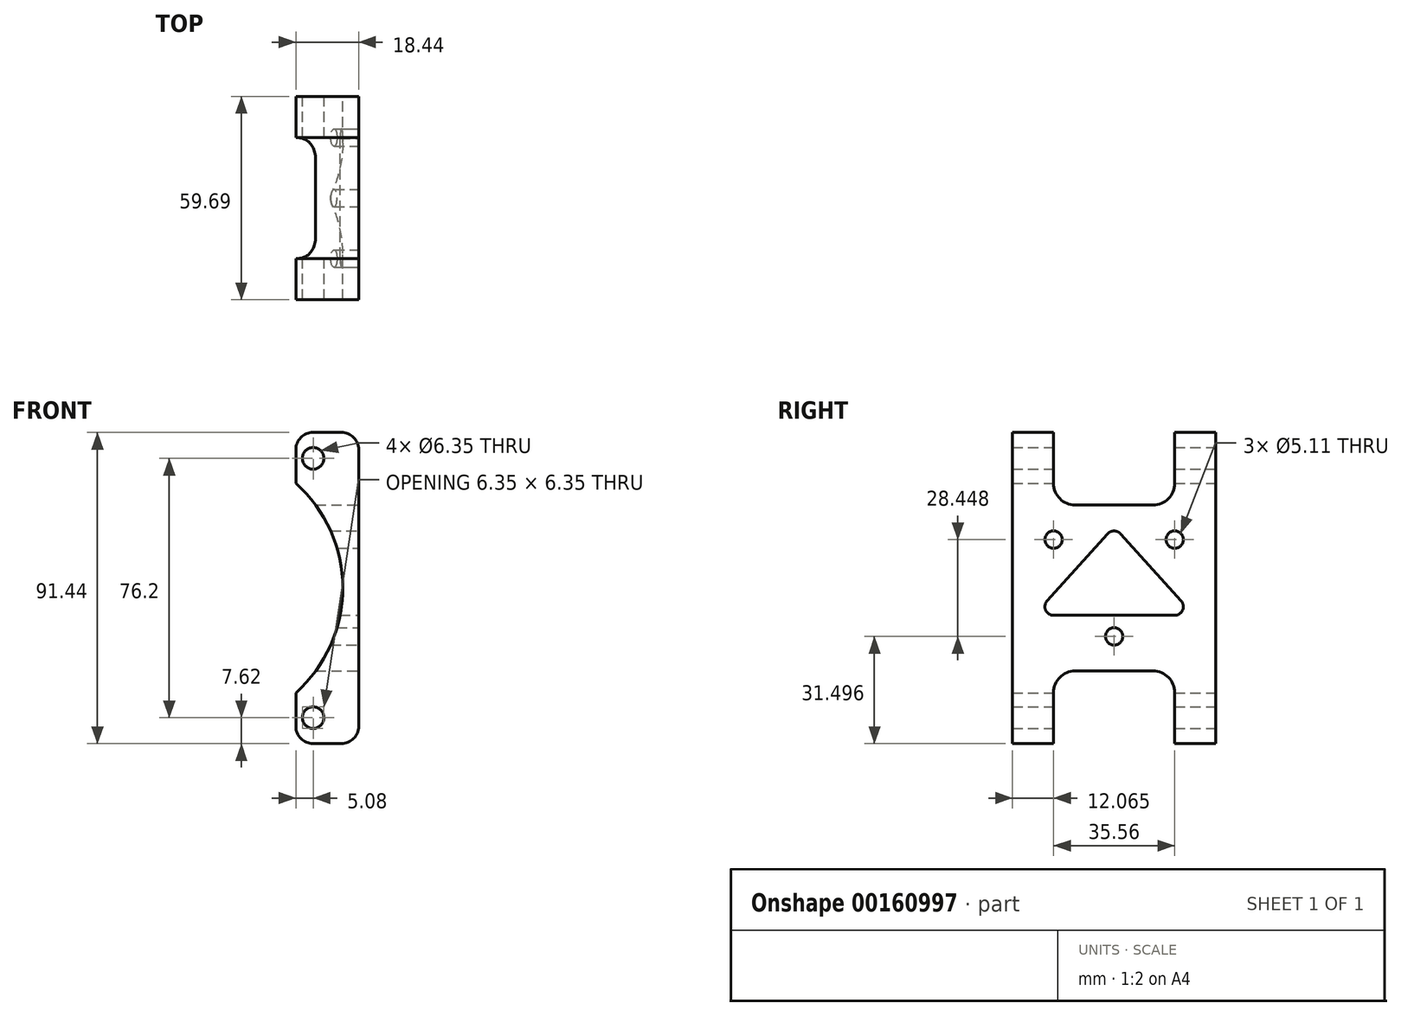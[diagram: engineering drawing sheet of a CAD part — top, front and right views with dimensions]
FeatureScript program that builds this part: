
annotation { "Feature Type Name" : "Feature", "Feature Type Description" : "" }
export const myFeature = defineFeature(function(context is Context, id is Id, definition is map)
    precondition{}
    {
        {
            var Q0;
            Q0=qCreatedBy(makeId("Front.planeOp"),FACE);
            var sketch = newSketch(context, id + "F0", { "sketchPlane" : qUnion([Q0])});
            skLineSegment(sketch, "E0.bottom", {"start": v(0, 0) * mm, "end": v(18.44, 0) * mm});
            skLineSegment(sketch, "E0.top", {"start": v(0, 91.44) * mm, "end": v(18.44, 91.44) * mm});
            skLineSegment(sketch, "E0.left", {"start": v(0, 0) * mm, "end": v(0, 19.33) * mm});
            skLineSegment(sketch, "E0.right", {"start": v(18.44, 0) * mm, "end": v(18.44, 91.44) * mm});
            skCircle(sketch, "E1", {"center": v(5.08, 83.82) * mm, "radius": 3.18 * mm});
            skCircle(sketch, "E2", {"center": v(5.08, 7.62) * mm, "radius": 3.18 * mm});
            skCircle(sketch, "E3", {"center": v(-27.48, 45.72) * mm, "radius": 38.1 * mm, "construction": true});
            skPoint(sketch, "E4.startSnap0", {"position": v(9.22, 91.44) * mm});
            skPoint(sketch, "E4.endSnap0", {"position": v(9.22, 0) * mm});
            skPoint(sketch, "E5", {"position": v(5.08, 45.72) * mm});
            skLineSegment(sketch, "E6", {"start": v(5.08, 83.82) * mm, "end": v(5.08, 7.62) * mm, "construction": true});
            skArc(sketch, "E7", {"start": v(0, 14.93) * mm, "mid": v(13.8, 45.72) * mm, "end": v(0, 76.51) * mm});
            skLineSegment(sketch, "E8.trimOffspring", {"start": v(0, 72.1) * mm, "end": v(0, 91.44) * mm});
            skSolve(sketch);
        }
        {
            var Q0;
            Q0 = qSketchRegion(id + "F0", true);
            extrude(context, id + "F1", {"entities" : qUnion([Q0]), "depth" : 59.69 * mm});
        }
        {
            var Q0;
            Q0=makeQuery(id+"F1.opExtrude","SWEPT_EDGE",EDGE,{"disambiguationData":[OSD([sQuery(id+"F0.wireOp",EDGE,"E0.top"),sQuery(id+"F0.wireOp",EDGE,"E8.trimOffspring")])]});
            var Q1;
            Q1=makeQuery(id+"F1.opExtrude","SWEPT_EDGE",EDGE,{"disambiguationData":[OSD([sQuery(id+"F0.wireOp",EDGE,"E0.bottom"),sQuery(id+"F0.wireOp",EDGE,"E0.left")])]});
            fillet(context, id + "F2", {"entities" : qUnion([Q0, Q1]), "radius" : 5.08 * mm, "tangentPropagation" : true, "allowEdgeOverflow" : false});
        }
        {
            var Q0;
            Q0=makeQuery(id+"F1.opExtrude","SWEPT_FACE",FACE,{"disambiguationData":[OSD([sQuery(id+"F0.wireOp",EDGE,"E0.right")])]});
            var sketch = newSketch(context, id + "F3", { "sketchPlane" : qUnion([Q0])});
            skLineSegment(sketch, "E9", {"start": v(-59.7, 45.72) * mm, "end": v(0, 45.72) * mm, "construction": true});
            skLineSegment(sketch, "E10", {"start": v(-29.85, 91.44) * mm, "end": v(-29.85, 0) * mm, "construction": true});
            skCircle(sketch, "E11", {"center": v(-47.62, 59.94) * mm, "radius": 2.55 * mm});
            skCircle(sketch, "E12", {"center": v(-12.07, 59.94) * mm, "radius": 2.55 * mm});
            skCircle(sketch, "E13", {"center": v(-29.85, 31.5) * mm, "radius": 2.55 * mm});
            skLineSegment(sketch, "E14.bottom", {"start": v(-47.63, 91.44) * mm, "end": v(-12.07, 91.44) * mm});
            skLineSegment(sketch, "E14.top", {"start": v(-41.27, 70.1) * mm, "end": v(-18.42, 70.1) * mm});
            skLineSegment(sketch, "E14.left", {"start": v(-47.62, 91.44) * mm, "end": v(-47.62, 76.45) * mm});
            skLineSegment(sketch, "E14.right", {"start": v(-12.07, 91.44) * mm, "end": v(-12.07, 76.45) * mm});
            skLineSegment(sketch, "E15.bottom", {"start": v(-47.62, 0) * mm, "end": v(-12.07, 0) * mm});
            skLineSegment(sketch, "E15.top", {"start": v(-41.27, 21.34) * mm, "end": v(-18.41, 21.34) * mm});
            skLineSegment(sketch, "E15.left", {"start": v(-47.62, 0) * mm, "end": v(-47.62, 14.99) * mm});
            skLineSegment(sketch, "E15.right", {"start": v(-12.07, 0) * mm, "end": v(-12.07, 14.99) * mm});
            skPoint(sketch, "E16.visualSharp", {"position": v(-47.62, 70.1) * mm});
            skArc(sketch, "E16.filletArc", {"start": v(-47.62, 76.45) * mm, "mid": v(-45.77, 71.96) * mm, "end": v(-41.27, 70.1) * mm});
            skPoint(sketch, "E17.visualSharp", {"position": v(-12.07, 70.1) * mm});
            skArc(sketch, "E17.filletArc", {"start": v(-18.42, 70.1) * mm, "mid": v(-13.92, 71.96) * mm, "end": v(-12.07, 76.45) * mm});
            skPoint(sketch, "E18.visualSharp", {"position": v(-47.62, 21.34) * mm});
            skArc(sketch, "E18.filletArc", {"start": v(-41.27, 21.34) * mm, "mid": v(-45.77, 19.48) * mm, "end": v(-47.63, 14.99) * mm});
            skPoint(sketch, "E19.visualSharp", {"position": v(-12.07, 21.34) * mm});
            skArc(sketch, "E19.filletArc", {"start": v(-12.06, 14.99) * mm, "mid": v(-13.92, 19.48) * mm, "end": v(-18.41, 21.34) * mm});
            skArc(sketch, "E20", {"start": v(-27.96, 61.64) * mm, "mid": v(-29.85, 62.48) * mm, "end": v(-31.73, 61.64) * mm});
            skArc(sketch, "E21", {"start": v(-49.51, 41.92) * mm, "mid": v(-49.9, 39.08) * mm, "end": v(-47.37, 37.7) * mm});
            skArc(sketch, "E22", {"start": v(-12.32, 37.7) * mm, "mid": v(-9.8, 39.08) * mm, "end": v(-10.18, 41.92) * mm});
            skLineSegment(sketch, "E23", {"start": v(-31.73, 61.64) * mm, "end": v(-49.51, 41.92) * mm});
            skLineSegment(sketch, "E24", {"start": v(-27.96, 61.64) * mm, "end": v(-10.18, 41.92) * mm});
            skLineSegment(sketch, "E25", {"start": v(-11.81, 37.7) * mm, "end": v(-47.37, 37.7) * mm});
            skSolve(sketch);
        }
        {
            var Q0;
            Q0 = qSketchRegion(id + "F3", true);
            extrude(context, id + "F4", {"entities" : qUnion([Q0]), "operationType" : NewBodyOperationType.REMOVE, "endBound" : BoundingType.THROUGH_ALL, "oppositeDirection" : true, "depth" : 25.4 * mm});
        }
        {
            var Q0;
            {var subQ0=sQuery(id+"F0.wireOp",EDGE,"E0.right");var subQ1=sQuery(id+"F0.wireOp",EDGE,"E0.top");Q0=makeQuery(id+"F4.boolean.opBoolean","SPLIT",EDGE,{"disambiguationData":[TD([makeQuery(id+"F4.opExtrude","SWEPT_FACE",FACE,{"disambiguationData":[OSD([sQuery(id+"F3.wireOp",EDGE,"E14.left")])]})])],"derivedFrom":makeQuery(id+"F1.opExtrude","SWEPT_EDGE",EDGE,{"disambiguationData":[OSD([subQ1,subQ0])]})});}
            var Q1;
            {var subQ0=sQuery(id+"F0.wireOp",EDGE,"E0.right");var subQ1=sQuery(id+"F0.wireOp",EDGE,"E0.top");Q1=makeQuery(id+"F4.boolean.opBoolean","SPLIT",EDGE,{"disambiguationData":[TD([makeQuery(id+"F4.opExtrude","SWEPT_FACE",FACE,{"disambiguationData":[OSD([sQuery(id+"F3.wireOp",EDGE,"E14.right")])]})])],"derivedFrom":makeQuery(id+"F1.opExtrude","SWEPT_EDGE",EDGE,{"disambiguationData":[OSD([subQ1,subQ0])]})});}
            var Q2;
            {var subQ0=sQuery(id+"F0.wireOp",EDGE,"E0.bottom");var subQ1=sQuery(id+"F0.wireOp",EDGE,"E0.right");Q2=makeQuery(id+"F4.boolean.opBoolean","SPLIT",EDGE,{"disambiguationData":[TD([makeQuery(id+"F4.opExtrude","SWEPT_FACE",FACE,{"disambiguationData":[OSD([sQuery(id+"F3.wireOp",EDGE,"E15.left")])]})])],"derivedFrom":makeQuery(id+"F1.opExtrude","SWEPT_EDGE",EDGE,{"disambiguationData":[OSD([subQ0,subQ1])]})});}
            var Q3;
            {var subQ0=sQuery(id+"F0.wireOp",EDGE,"E0.bottom");var subQ1=sQuery(id+"F0.wireOp",EDGE,"E0.right");Q3=makeQuery(id+"F4.boolean.opBoolean","SPLIT",EDGE,{"disambiguationData":[TD([makeQuery(id+"F4.opExtrude","SWEPT_FACE",FACE,{"disambiguationData":[OSD([sQuery(id+"F3.wireOp",EDGE,"E15.right")])]})])],"derivedFrom":makeQuery(id+"F1.opExtrude","SWEPT_EDGE",EDGE,{"disambiguationData":[OSD([subQ0,subQ1])]})});}
            fillet(context, id + "F5", {"entities" : qUnion([Q0, Q1, Q2, Q3]), "radius" : 5.08 * mm, "tangentPropagation" : true, "allowEdgeOverflow" : false});
        }
    });
